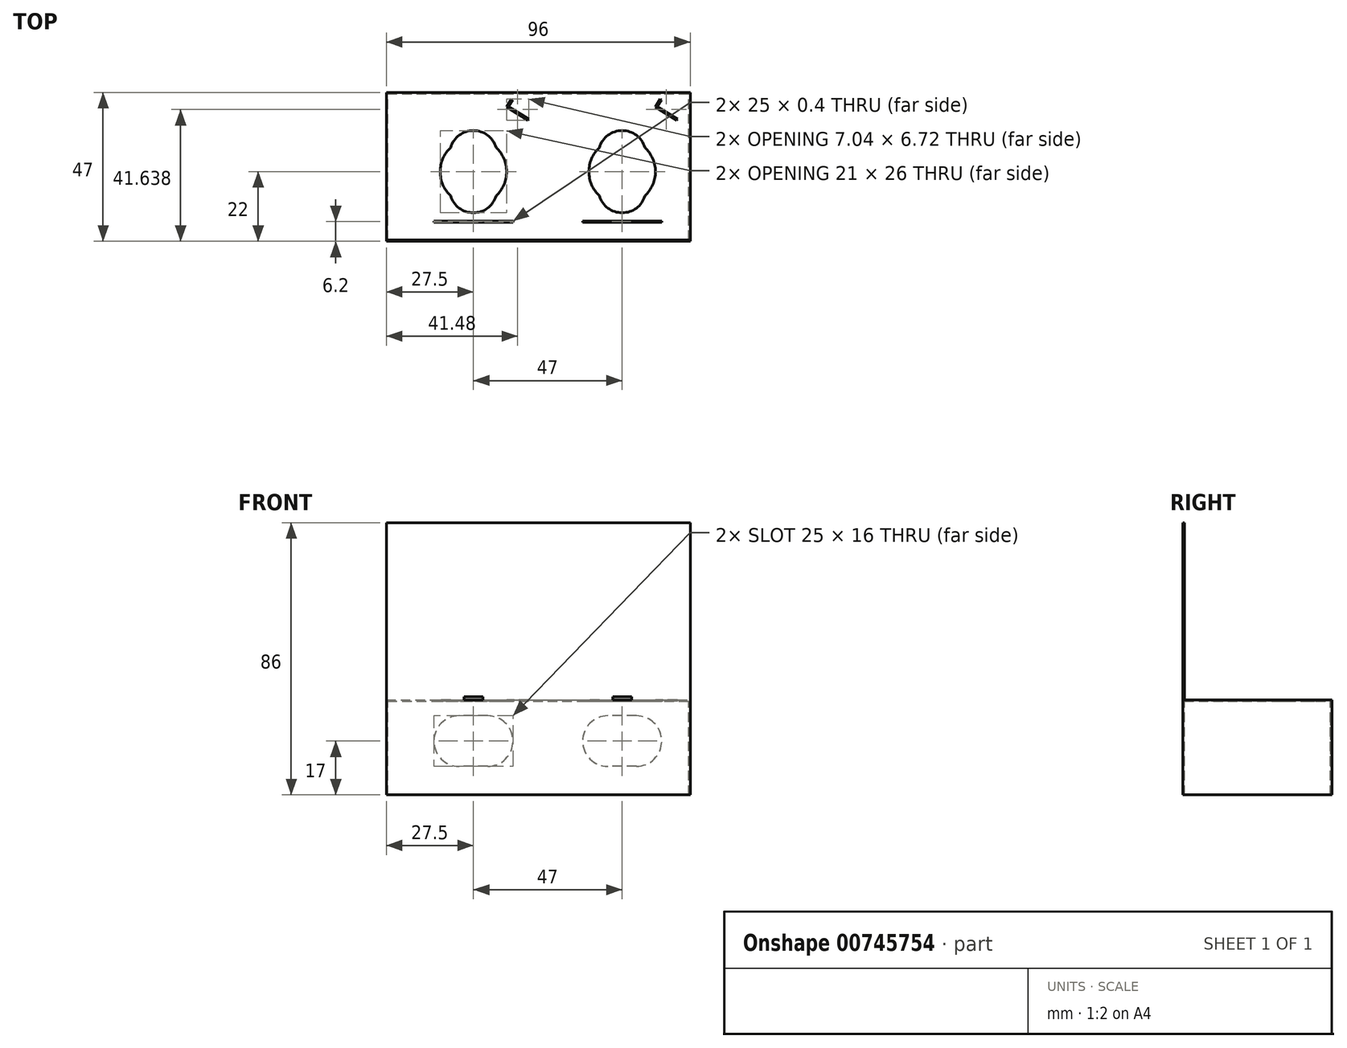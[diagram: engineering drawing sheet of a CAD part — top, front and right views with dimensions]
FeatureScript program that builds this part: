
annotation { "Feature Type Name" : "Feature", "Feature Type Description" : "" }
export const myFeature = defineFeature(function(context is Context, id is Id, definition is map)
    precondition{}
    {
        {
            var Q0;
            Q0=qCreatedBy(makeId("Right.planeOp"),FACE);
            var sketch = newSketch(context, id + "F0", { "sketchPlane" : qUnion([Q0])});
            skLineSegment(sketch, "E0.bottom", {"start": v(0, 0) * mm, "end": v(47, 0) * mm});
            skLineSegment(sketch, "E0.top", {"start": v(0.4, 30) * mm, "end": v(47, 30) * mm});
            skLineSegment(sketch, "E0.left", {"start": v(0, 0) * mm, "end": v(0, 30) * mm});
            skLineSegment(sketch, "E0.right", {"start": v(47, 0) * mm, "end": v(47, 30) * mm});
            skLineSegment(sketch, "E1", {"start": v(0, 30) * mm, "end": v(0, 86) * mm});
            skLineSegment(sketch, "E2", {"start": v(0, 86) * mm, "end": v(0.4, 86) * mm});
            skLineSegment(sketch, "E3", {"start": v(0.4, 86) * mm, "end": v(0.4, 30) * mm});
            skSolve(sketch);
        }
        {
            var Q0;
            Q0 = qSketchRegion(id + "F0", true);
            extrude(context, id + "F1", {"entities" : qUnion([Q0]), "oppositeDirection" : true, "depth" : 96 * mm, "offsetDistance" : 25 * mm});
        }
        {
            var Q0;
            Q0=makeQuery(id+"F1.opExtrude","SWEPT_FACE",FACE,{"disambiguationData":[OSD([sQuery(id+"F0.wireOp",EDGE,"E0.bottom")])]});
            shell(context, id + "F2", {"entities" : qUnion([Q0]), "thickness" : 0.4 * mm});
        }
        {
            var Q0;
            Q0=makeQuery(id+"F1.opExtrude","SWEPT_FACE",FACE,{"disambiguationData":[OSD([sQuery(id+"F0.wireOp",EDGE,"E0.top")])]});
            var sketch = newSketch(context, id + "F3", { "sketchPlane" : qUnion([Q0])});
            skLineSegment(sketch, "E4", {"start": v(-68.5, 42.28) * mm, "end": v(-68.5, 5.68) * mm, "construction": true});
            skLineSegment(sketch, "E5", {"start": v(-77.33, 27.5) * mm, "end": v(-56.56, 27.5) * mm, "construction": true});
            skLineSegment(sketch, "E6", {"start": v(-71.95, 16.5) * mm, "end": v(-63.05, 16.5) * mm, "construction": true});
            skLineSegment(sketch, "E7", {"start": v(-76.32, 22) * mm, "end": v(-61.17, 22) * mm, "construction": true});
            skArc(sketch, "E8", {"start": v(-61.32, 14.34) * mm, "mid": v(-58, 22) * mm, "end": v(-61.32, 29.66) * mm});
            skLineSegment(sketch, "E9.bottom", {"start": v(-81, 6.4) * mm, "end": v(-56, 6.4) * mm});
            skLineSegment(sketch, "E9.top", {"start": v(-81, 6) * mm, "end": v(-56, 6) * mm});
            skLineSegment(sketch, "E9.left", {"start": v(-81, 6.4) * mm, "end": v(-81, 6) * mm});
            skLineSegment(sketch, "E9.right", {"start": v(-56, 6.4) * mm, "end": v(-56, 6) * mm});
            skArc(sketch, "E10.trimOffspring", {"start": v(-61.32, 29.66) * mm, "mid": v(-68.5, 35) * mm, "end": v(-75.68, 29.66) * mm});
            skArc(sketch, "E11.trimOffspring", {"start": v(-75.68, 14.34) * mm, "mid": v(-68.5, 9) * mm, "end": v(-61.32, 14.34) * mm});
            skArc(sketch, "E12.trimOffspring", {"start": v(-75.68, 29.66) * mm, "mid": v(-79, 22) * mm, "end": v(-75.68, 14.34) * mm});
            skLineSegment(sketch, "E13", {"start": v(-48, 53.48) * mm, "end": v(-48, -13) * mm, "construction": true});
            skLineSegment(sketch, "E14", {"start": v(-51, 38.62) * mm, "end": v(-57.5, 42.57) * mm});
            skLineSegment(sketch, "E15", {"start": v(-57.5, 42.57) * mm, "end": v(-56.14, 44.8) * mm});
            skLineSegment(sketch, "E16", {"start": v(-56.14, 44.8) * mm, "end": v(-56.48, 45) * mm});
            skLineSegment(sketch, "E17", {"start": v(-56.48, 45) * mm, "end": v(-58.04, 42.44) * mm});
            skLineSegment(sketch, "E18", {"start": v(-51, 38.62) * mm, "end": v(-51.2, 38.28) * mm});
            skLineSegment(sketch, "E19", {"start": v(-51.2, 38.28) * mm, "end": v(-58.04, 42.44) * mm});
            skArc(sketch, "E20.1.0.0", {"start": v(-14.32, 29.66) * mm, "mid": v(-21.5, 35) * mm, "end": v(-28.68, 29.66) * mm});
            skArc(sketch, "E20.1.0.1", {"start": v(-28.68, 29.66) * mm, "mid": v(-32, 22) * mm, "end": v(-28.68, 14.34) * mm});
            skArc(sketch, "E20.1.0.2", {"start": v(-28.68, 14.34) * mm, "mid": v(-21.5, 9) * mm, "end": v(-14.32, 14.34) * mm});
            skArc(sketch, "E20.1.0.3", {"start": v(-14.32, 14.34) * mm, "mid": v(-11, 22) * mm, "end": v(-14.32, 29.66) * mm});
            skLineSegment(sketch, "E20.1.0.4", {"start": v(-9, 6.4) * mm, "end": v(-9, 6) * mm});
            skLineSegment(sketch, "E20.1.0.5", {"start": v(-34, 6) * mm, "end": v(-9, 6) * mm});
            skLineSegment(sketch, "E20.1.0.6", {"start": v(-34, 6.4) * mm, "end": v(-9, 6.4) * mm});
            skLineSegment(sketch, "E20.1.0.7", {"start": v(-34, 6.4) * mm, "end": v(-34, 6) * mm});
            skLineSegment(sketch, "E20.1.0.8", {"start": v(-21.5, 42.28) * mm, "end": v(-21.5, 5.68) * mm, "construction": true});
            skLineSegment(sketch, "E20.1.0.9", {"start": v(-4.2, 38.28) * mm, "end": v(-11.04, 42.44) * mm});
            skLineSegment(sketch, "E20.1.0.10", {"start": v(-4, 38.62) * mm, "end": v(-10.5, 42.57) * mm});
            skLineSegment(sketch, "E20.1.0.11", {"start": v(-4, 38.62) * mm, "end": v(-4.2, 38.28) * mm});
            skLineSegment(sketch, "E20.1.0.12", {"start": v(-10.5, 42.57) * mm, "end": v(-9.14, 44.8) * mm});
            skLineSegment(sketch, "E20.1.0.13", {"start": v(-9.48, 45) * mm, "end": v(-11.04, 42.44) * mm});
            skLineSegment(sketch, "E20.1.0.14", {"start": v(-9.14, 44.8) * mm, "end": v(-9.48, 45) * mm});
            skLineSegment(sketch, "E20.direction1", {"start": v(-75.68, 29.66) * mm, "end": v(-28.68, 29.66) * mm, "construction": true});
            skSolve(sketch);
        }
        {
            var Q0;
            Q0 = qSketchRegion(id + "F3", true);
            var Q1;
            Q1=makeQuery(id+"F2.opShell","OFFSET_FACE",FACE,{"disambiguationData":[OSD([sQuery(id+"F0.wireOp",EDGE,"E0.top")])]});
            extrude(context, id + "F4", {"entities" : qUnion([Q0]), "operationType" : NewBodyOperationType.REMOVE, "endBound" : BoundingType.UP_TO_SURFACE, "oppositeDirection" : true, "depth" : 25 * mm, "endBoundEntityFace" : qUnion([Q1]), "offsetDistance" : 25 * mm});
        }
        {
            var Q0;
            Q0=makeQuery(id+"F1.opExtrude","SWEPT_FACE",FACE,{"disambiguationData":[OSD([sQuery(id+"F0.wireOp",EDGE,"E0.right")])]});
            var sketch = newSketch(context, id + "F5", { "sketchPlane" : qUnion([Q0])});
            skArc(sketch, "E21", {"start": v(73, 9) * mm, "mid": v(81, 17) * mm, "end": v(73, 25) * mm});
            skArc(sketch, "E22", {"start": v(64, 25) * mm, "mid": v(56, 17) * mm, "end": v(64, 9) * mm});
            skLineSegment(sketch, "E23", {"start": v(64, 25) * mm, "end": v(73, 25) * mm});
            skLineSegment(sketch, "E24", {"start": v(64, 9) * mm, "end": v(73, 9) * mm});
            skLineSegment(sketch, "E25", {"start": v(68.5, 27.98) * mm, "end": v(68.5, 5.96) * mm, "construction": true});
            skPoint(sketch, "E25.startSnap0", {"position": v(68.5, 25) * mm});
            skPoint(sketch, "E25.endSnap0", {"position": v(68.5, 9) * mm});
            skLineSegment(sketch, "E26.bottom", {"start": v(65.5, 30) * mm, "end": v(71.5, 30) * mm});
            skLineSegment(sketch, "E26.top", {"start": v(65.5, 31) * mm, "end": v(71.5, 31) * mm});
            skLineSegment(sketch, "E26.left", {"start": v(65.5, 30) * mm, "end": v(65.5, 31) * mm});
            skLineSegment(sketch, "E26.right", {"start": v(71.5, 30) * mm, "end": v(71.5, 31) * mm});
            skArc(sketch, "E27.1.0.0", {"start": v(26, 9) * mm, "mid": v(34, 17) * mm, "end": v(26, 25) * mm});
            skLineSegment(sketch, "E27.1.0.1", {"start": v(17, 25) * mm, "end": v(26, 25) * mm});
            skArc(sketch, "E27.1.0.2", {"start": v(17, 25) * mm, "mid": v(9, 17) * mm, "end": v(17, 9) * mm});
            skLineSegment(sketch, "E27.1.0.3", {"start": v(17, 9) * mm, "end": v(26, 9) * mm});
            skLineSegment(sketch, "E27.1.0.4", {"start": v(21.5, 27.98) * mm, "end": v(21.5, 5.96) * mm, "construction": true});
            skLineSegment(sketch, "E27.1.0.5", {"start": v(18.5, 31) * mm, "end": v(24.5, 31) * mm});
            skLineSegment(sketch, "E27.1.0.6", {"start": v(18.5, 30) * mm, "end": v(24.5, 30) * mm});
            skLineSegment(sketch, "E27.1.0.7", {"start": v(24.5, 30) * mm, "end": v(24.5, 31) * mm});
            skLineSegment(sketch, "E27.1.0.8", {"start": v(18.5, 30) * mm, "end": v(18.5, 31) * mm});
            skLineSegment(sketch, "E27.direction1", {"start": v(64, 9) * mm, "end": v(17, 9) * mm, "construction": true});
            skSolve(sketch);
        }
        {
            var Q0;
            Q0=makeQuery(id+"F5.imprint","IMPRINT",FACE,{"disambiguationData":[TD([[makeQuery(id+"F5.imprint","IMPRINT",EDGE,{"derivedFrom":sQuery(id+"F5.wireOp",EDGE,"E27.1.0.0")}),1.0]])]});
            var Q1;
            Q1=makeQuery(id+"F5.imprint","IMPRINT",FACE,{"disambiguationData":[TD([[makeQuery(id+"F5.imprint","IMPRINT",EDGE,{"derivedFrom":sQuery(id+"F5.wireOp",EDGE,"E21")}),1.0]])]});
            var Q2;
            Q2=makeQuery(id+"F2.opShell","OFFSET_FACE",FACE,{"disambiguationData":[OSD([sQuery(id+"F0.wireOp",EDGE,"E0.right")])]});
            extrude(context, id + "F6", {"entities" : qUnion([Q0, Q1]), "operationType" : NewBodyOperationType.REMOVE, "endBound" : BoundingType.UP_TO_SURFACE, "oppositeDirection" : true, "depth" : 25 * mm, "endBoundEntityFace" : qUnion([Q2]), "offsetDistance" : 25 * mm});
        }
        {
            var Q0;
            Q0=makeQuery(id+"F5.imprint","IMPRINT",FACE,{"disambiguationData":[TD([[makeQuery(id+"F5.imprint","IMPRINT",EDGE,{"derivedFrom":sQuery(id+"F5.wireOp",EDGE,"E27.1.0.5")}),-1.0]])]});
            var Q1;
            Q1=makeQuery(id+"F5.imprint","IMPRINT",FACE,{"disambiguationData":[TD([[makeQuery(id+"F5.imprint","IMPRINT",EDGE,{"derivedFrom":sQuery(id+"F5.wireOp",EDGE,"E26.bottom")}),-1.0]])]});
            var Q2;
            Q2=makeQuery(id+"F1.opExtrude","SWEPT_FACE",FACE,{"disambiguationData":[OSD([sQuery(id+"F0.wireOp",EDGE,"E0.left"),sQuery(id+"F0.wireOp",EDGE,"E1")])]});
            extrude(context, id + "F7", {"entities" : qUnion([Q0, Q1]), "operationType" : NewBodyOperationType.REMOVE, "endBound" : BoundingType.UP_TO_SURFACE, "oppositeDirection" : true, "depth" : 25 * mm, "endBoundEntityFace" : qUnion([Q2]), "offsetDistance" : 25 * mm});
        }
    });
